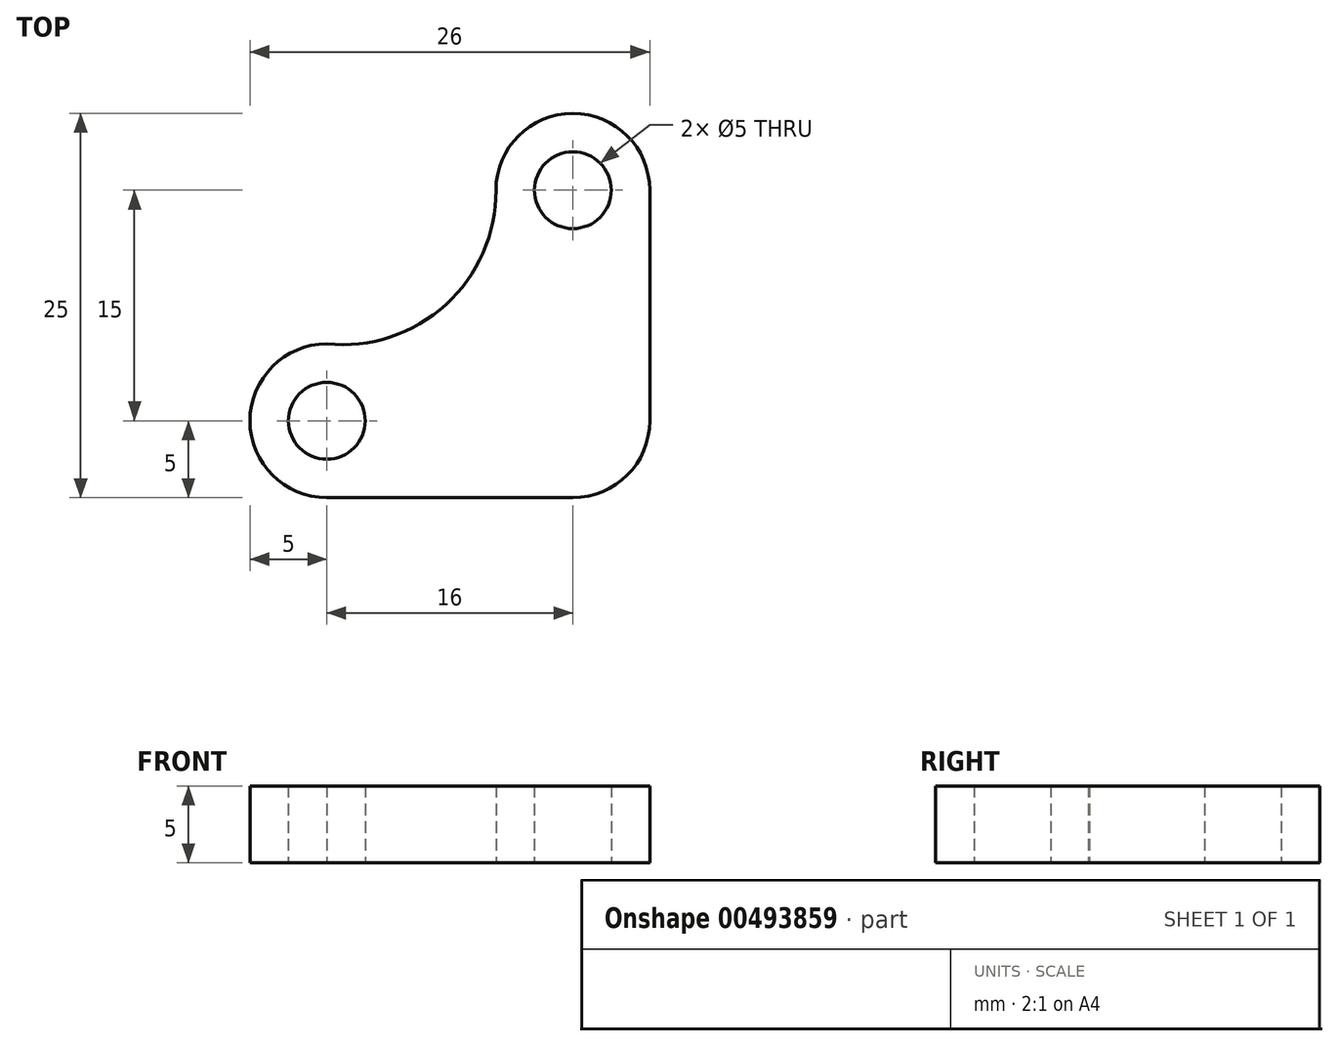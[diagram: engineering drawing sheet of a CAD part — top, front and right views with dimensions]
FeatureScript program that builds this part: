
annotation { "Feature Type Name" : "Feature", "Feature Type Description" : "" }
export const myFeature = defineFeature(function(context is Context, id is Id, definition is map)
    precondition{}
    {
        {
            var Q0;
            Q0=qCreatedBy(makeId("Top.planeOp"),FACE);
            var sketch = newSketch(context, id + "F0", { "sketchPlane" : qUnion([Q0])});
            skArc(sketch, "E0", {"start": v(0, -5) * mm, "mid": v(3.54, -3.54) * mm, "end": v(5, 0) * mm});
            skLineSegment(sketch, "E1", {"start": v(0, -5) * mm, "end": v(-16, -5) * mm});
            skLineSegment(sketch, "E2", {"start": v(5, 0) * mm, "end": v(5, 15) * mm});
            skArc(sketch, "E3", {"start": v(5, 15) * mm, "mid": v(0, 20) * mm, "end": v(-5, 15) * mm});
            skArc(sketch, "E4", {"start": v(-16, 5) * mm, "mid": v(-8.27, 7.55) * mm, "end": v(-5, 15) * mm});
            skArc(sketch, "E5", {"start": v(-16, 5) * mm, "mid": v(-21, 0) * mm, "end": v(-16, -5) * mm});
            skCircle(sketch, "E6", {"center": v(0, 15) * mm, "radius": 2.5 * mm});
            skCircle(sketch, "E7", {"center": v(-16, 0) * mm, "radius": 2.5 * mm});
            skSolve(sketch);
        }
        {
            var Q0;
            Q0=makeQuery(id+"F0.imprint","IMPRINT",FACE,{"disambiguationData":[TD([[makeQuery(id+"F0.imprint","IMPRINT",EDGE,{"derivedFrom":sQuery(id+"F0.wireOp",EDGE,"E0")}),1.0]])]});
            extrude(context, id + "F1", {"entities" : qUnion([Q0]), "depth" : 5 * mm});
        }
    });
